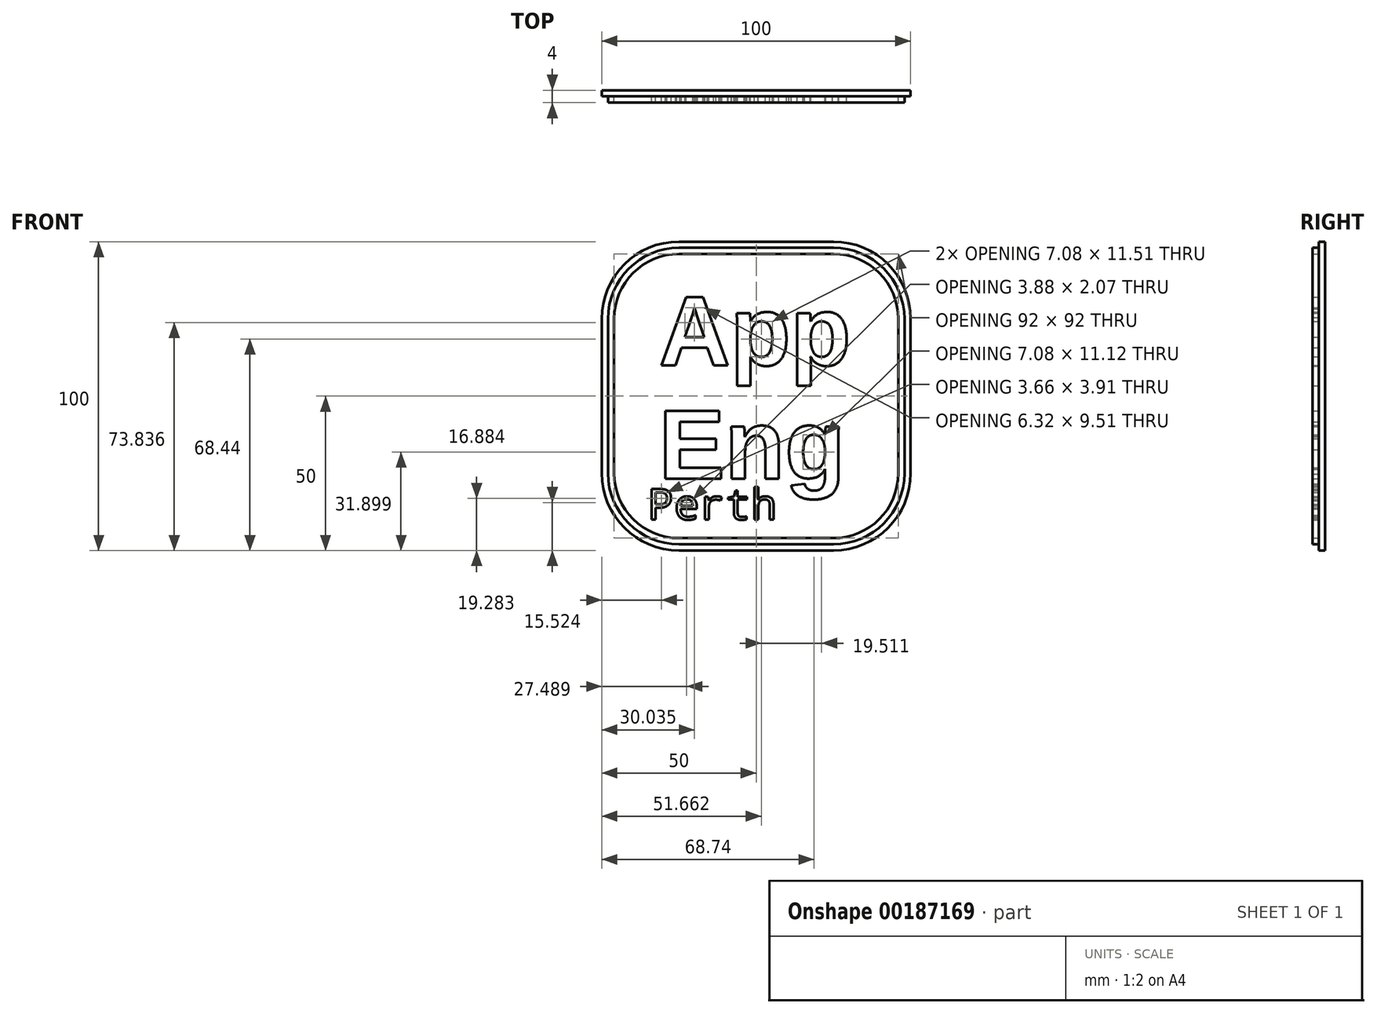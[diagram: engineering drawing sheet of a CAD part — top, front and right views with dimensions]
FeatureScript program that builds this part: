
annotation { "Feature Type Name" : "Feature", "Feature Type Description" : "" }
export const myFeature = defineFeature(function(context is Context, id is Id, definition is map)
    precondition{}
    {
        {
            var Q0;
            Q0=qCreatedBy(makeId("Front.planeOp"),FACE);
            cPlane(context, id + "F0", {"entities" : qUnion([Q0]), "cplaneType" : CPlaneType.OFFSET, "offset" : 2 * mm, "width" : 152.4 * mm, "height" : 152.4 * mm});
        }
        {
            var Q0;
            Q0=qCreatedBy(makeId("Front.planeOp"),FACE);
            var sketch = newSketch(context, id + "F1", { "sketchPlane" : qUnion([Q0])});
            skLineSegment(sketch, "E0.bottom", {"start": v(25, -50) * mm, "end": v(-25, -50) * mm});
            skLineSegment(sketch, "E0.top", {"start": v(25, 50) * mm, "end": v(-25, 50) * mm});
            skLineSegment(sketch, "E0.left", {"start": v(50, -25) * mm, "end": v(50, 25) * mm});
            skLineSegment(sketch, "E0.right", {"start": v(-50, -25) * mm, "end": v(-50, 25) * mm});
            skPoint(sketch, "E0.middle", {"position": v(0, 0) * mm});
            skArc(sketch, "E1.filletArc", {"start": v(50, 25) * mm, "mid": v(42.68, 42.68) * mm, "end": v(25, 50) * mm});
            skArc(sketch, "E2.filletArc", {"start": v(25, -50) * mm, "mid": v(42.68, -42.68) * mm, "end": v(50, -25) * mm});
            skArc(sketch, "E3.filletArc", {"start": v(-50, -25) * mm, "mid": v(-42.68, -42.68) * mm, "end": v(-25, -50) * mm});
            skArc(sketch, "E4.filletArc", {"start": v(-25, 50) * mm, "mid": v(-42.68, 42.68) * mm, "end": v(-50, 25) * mm});
            skSolve(sketch);
        }
        {
            var Q0;
            Q0=makeQuery(id+"F1.imprint","IMPRINT",FACE,{"disambiguationData":[TD([[makeQuery(id+"F1.imprint","IMPRINT",EDGE,{"derivedFrom":sQuery(id+"F1.wireOp",EDGE,"E0.bottom")}),-1.0]])]});
            var Q1;
            Q1=qCreatedBy(id+"F0.planeOp",FACE);
            extrude(context, id + "F2", {"entities" : qUnion([Q0]), "endBound" : BoundingType.UP_TO_SURFACE, "endBoundEntityFace" : qUnion([Q1]), "depth" : 5.08 * mm});
        }
        {
            var Q0;
            Q0=qCreatedBy(id+"F0.planeOp",FACE);
            var sketch = newSketch(context, id + "F3", { "sketchPlane" : qUnion([Q0])});
            skLineSegment(sketch, "E5.bottom", {"start": v(25, -48) * mm, "end": v(-25, -48) * mm});
            skLineSegment(sketch, "E5.top", {"start": v(25, 48) * mm, "end": v(-25, 48) * mm});
            skLineSegment(sketch, "E5.left", {"start": v(48, -25) * mm, "end": v(48, 25) * mm});
            skLineSegment(sketch, "E5.right", {"start": v(-48, -25) * mm, "end": v(-48, 25) * mm});
            skPoint(sketch, "E5.middle", {"position": v(0, 0) * mm});
            skPoint(sketch, "E6.visualSharp", {"position": v(-48, 48) * mm});
            skArc(sketch, "E6.filletArc", {"start": v(-25, 48) * mm, "mid": v(-41.26, 41.26) * mm, "end": v(-48, 25) * mm});
            skPoint(sketch, "E7.visualSharp", {"position": v(-48, -48) * mm});
            skArc(sketch, "E7.filletArc", {"start": v(-48, -25) * mm, "mid": v(-41.26, -41.26) * mm, "end": v(-25, -48) * mm});
            skPoint(sketch, "E8.visualSharp", {"position": v(48, 48) * mm});
            skArc(sketch, "E8.filletArc", {"start": v(48, 25) * mm, "mid": v(41.26, 41.26) * mm, "end": v(25, 48) * mm});
            skPoint(sketch, "E9.visualSharp", {"position": v(48, -48) * mm});
            skArc(sketch, "E9.filletArc", {"start": v(25, -48) * mm, "mid": v(41.26, -41.26) * mm, "end": v(48, -25) * mm});
            skLineSegment(sketch, "E10.bottom", {"start": v(-25, 46) * mm, "end": v(25, 46) * mm});
            skLineSegment(sketch, "E10.top", {"start": v(-25, -46) * mm, "end": v(25, -46) * mm});
            skLineSegment(sketch, "E10.left", {"start": v(-46, 25) * mm, "end": v(-46, -25) * mm});
            skLineSegment(sketch, "E10.right", {"start": v(46, 25) * mm, "end": v(46, -25) * mm});
            skPoint(sketch, "E11.visualSharp", {"position": v(-46, 46) * mm});
            skArc(sketch, "E11.filletArc", {"start": v(-25, 46) * mm, "mid": v(-39.85, 39.85) * mm, "end": v(-46, 25) * mm});
            skPoint(sketch, "E12.visualSharp", {"position": v(-46, -46) * mm});
            skArc(sketch, "E12.filletArc", {"start": v(-46, -25) * mm, "mid": v(-39.85, -39.85) * mm, "end": v(-25, -46) * mm});
            skPoint(sketch, "E13.visualSharp", {"position": v(46, -46) * mm});
            skArc(sketch, "E13.filletArc", {"start": v(25, -46) * mm, "mid": v(39.85, -39.85) * mm, "end": v(46, -25) * mm});
            skPoint(sketch, "E14.visualSharp", {"position": v(46, 46) * mm});
            skArc(sketch, "E14.filletArc", {"start": v(46, 25) * mm, "mid": v(39.85, 39.85) * mm, "end": v(25, 46) * mm});
            skSolve(sketch);
        }
        {
            var Q0;
            Q0 = qSketchRegion(id + "F3", true);
            extrude(context, id + "F4", {"entities" : qUnion([Q0]), "depth" : 2 * mm});
        }
        {
            var Q0;
            Q0=qCreatedBy(id+"F0.planeOp",FACE);
            var sketch = newSketch(context, id + "F5", { "sketchPlane" : qUnion([Q0])});
            skText(sketch, "E15", { "text": "App\nEng", "fontName": "Arimo-Bold.ttf"});
            const initialGuessF5  = {"E15": [-0.0315, 0.01, 1, 0, 0.023]};
            skSetInitialGuess(sketch, initialGuessF5);
            skSolve(sketch);
        }
        {
            var Q0;
            Q0 = qSketchRegion(id + "F5", true);
            extrude(context, id + "F6", {"entities" : qUnion([Q0]), "depth" : 2 * mm});
        }
        {
            var Q0;
            Q0=qCreatedBy(id+"F0.planeOp",FACE);
            var sketch = newSketch(context, id + "F7", { "sketchPlane" : qUnion([Q0])});
            skText(sketch, "E16", { "text": "Perth", "fontName": "DroidSansMono.ttf"});
            const initialGuessF7  = {"E16": [-0.035, -0.04, 1, 0, 0.01]};
            skSetInitialGuess(sketch, initialGuessF7);
            skSolve(sketch);
        }
        {
            var Q0;
            Q0 = qSketchRegion(id + "F7", true);
            extrude(context, id + "F8", {"entities" : qUnion([Q0]), "depth" : 2 * mm});
        }
    });
